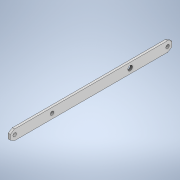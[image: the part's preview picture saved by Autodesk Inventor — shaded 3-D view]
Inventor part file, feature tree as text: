
AUTODESK INVENTOR PART (.ipt)
format: ipt  version: 2020 (Build 240168000, 168)  size: 217,600 bytes
history: native  units: in
note: dims shown in document units (in); Inventor stores cm internally (conversion verified against a paired STEP export)
features: extrude x5, sketch x5, other x3, projected_geometry x3
ambient origin geometry x8: Origin, YZ Plane, XZ Plane, XY Plane, X Axis, Y Axis, Z Axis, Center Point
bodies: Solid1 (feature_tree)
feature tree (16):
  other  "HexWheelGuard.ipt"
  extrude  "Extrusion1"  TaperAngle=0.0deg  [1 undecoded]
  extrude  "Extrusion2"  Depth=0.3937in
  extrude  "Extrusion3"  Depth=0.3937in TaperAngle=0.0deg
  extrude  "Extrusion4"  Depth=0.3543in
  extrude  "Extrusion5"  Depth=0.0787in
  other  "Solid1::HexWheelGuard.ipt"
  other  "TaggingFeature1"
  sketch  "Sketch1"  dims[d0=0.3937in d1=0.0in d2=0.0in]
  projected_geometry  "Projected Loop1"
  sketch  "Sketch2"  dims[d3=0.3937in d4=0.0in d5=0.122in]
  sketch  "Sketch3"  dims[d6=0.122in d7=0.3937in d8=0.0in]
  sketch  "Sketch4"  dims[d10=0.3937in d11=0.0in d12=0.3543in]
  projected_geometry  "Projected Loop2"
  sketch  "Sketch5"  dims[d13=0.0787in d14=0.0in d15=0.122in d17=1.5748in d18=0.5906in]
  projected_geometry  "Projected Loop3"
note: 1 required parameter value undecoded (feature->parameter linkage not recoverable at this tier; creation-order binding heuristic only, values carry confidence <= 0.55)
